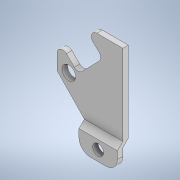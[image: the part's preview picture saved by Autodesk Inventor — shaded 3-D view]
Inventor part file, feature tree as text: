
AUTODESK INVENTOR PART (.ipt)
format: ipt  version: 2020 (Build 240168000, 168)  size: 261,120 bytes
history: native  units: mm
features: extrude x6, sketch x6, fillet x3, chamfer x2, projected_geometry x2, mirror x1
ambient origin geometry x8: Origin, YZ Plane, XZ Plane, XY Plane, X Axis, Y Axis, Z Axis, Center Point
bodies: Solid1 (feature_tree)
feature tree (20):
  extrude  "Extrusion1"  TaperAngle=0.0deg  [1 undecoded]
  extrude  "Extrusion5"  Depth=5.0mm
  fillet  "Fillet2"  Radius=2.5mm
  extrude  "Extrusion6"  Depth=1.0mm
  chamfer  "Chamfer1"  Distance=0.1mm
  extrude  "Extrusion7"  Depth=1.0mm
  chamfer  "Chamfer2"  [1 undecoded]
  extrude  "Extrusion8"  Depth=1.0mm
  extrude  "Extrusion9"  Depth=2.0mm
  fillet  "Fillet3"  Radius=3.525mm
  fillet  "Fillet4"  Radius=2.6mm
  mirror  "Mirror2"
  sketch  "Sketch1"  dims[d6=1.0mm d7=0.0mm]
  sketch  "Sketch7"  dims[d26=4.95mm d27=7.25mm d28=2.5mm d29=4.9mm d30=14.9mm d31=5.1mm d32=5.1mm d33=90.0deg d34=135.0deg d36=0.0mm d37=0.0mm]
  projected_geometry  "Projected Loop2"
  sketch  "Sketch8"  dims[d38=2.5mm d39=5.0mm d40=2.5mm]
  sketch  "Sketch9"  dims[d41=1.0mm d42=7.5mm]
  projected_geometry  "Projected Loop3"
  sketch  "Sketch10"  dims[d43=0.15mm]
  sketch  "Sketch11"  dims[d44=0.15mm d54=0.1mm d55=0.1mm d56=0.0mm d57=4.5mm d58=2.0mm d59=3.525mm d60=2.6mm d61=2.0mm d62=0.0mm d63=5.0mm d64=45.0deg d65=5.0mm d66=45.0deg d67=2.1mm d68=0.2mm d69=0.1mm d70=10.0mm d71=0.0mm d72=1.0mm d73=2.0mm d74=45.0deg d75=1.0mm d76=0.0mm d77=1.0mm d78=2.0mm d79=45.0deg d80=3.8mm d81=1.0mm d82=0.0mm d83=7.0mm d85=6.5mm d86=3.5mm d87=1.0mm d88=0.0mm d89=6.5mm d90=1.0mm d91=1.0mm d5=0.5mm d8=0.872665mm d11=0.5mm d12=0.872665mm d13=0.5mm d14=0.872665mm d25=0.5mm]
note: 2 required parameter values undecoded (feature->parameter linkage not recoverable at this tier; creation-order binding heuristic only, values carry confidence <= 0.55)
